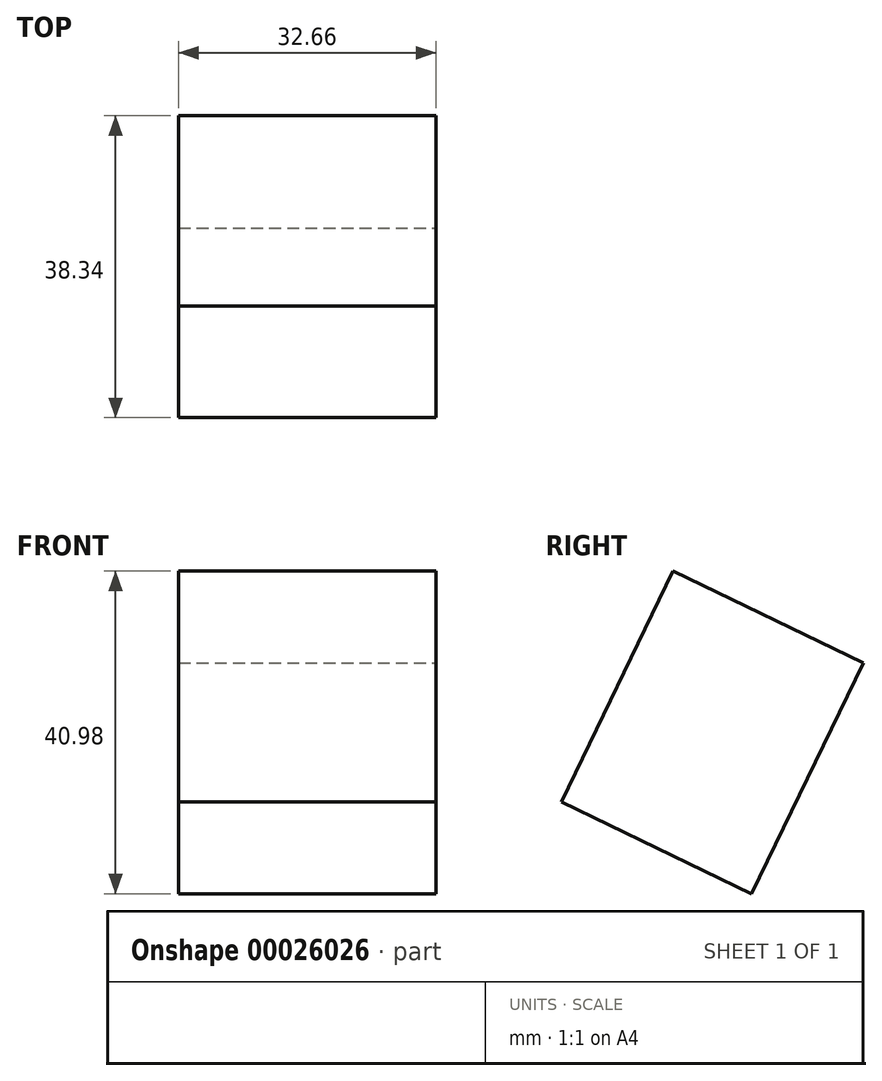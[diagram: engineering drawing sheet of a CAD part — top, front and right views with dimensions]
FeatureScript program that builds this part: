
annotation { "Feature Type Name" : "Feature", "Feature Type Description" : "" }
export const myFeature = defineFeature(function(context is Context, id is Id, definition is map)
    precondition{}
    {
        {
            var Q0;
            Q0=qCreatedBy(makeId("Right.planeOp"),FACE);
            var sketch = newSketch(context, id + "F0", { "sketchPlane" : qUnion([Q0])});
            skLineSegment(sketch, "E0", {"start": v(-66.15, 37.6) * mm, "end": v(-41.97, 25.94) * mm});
            skLineSegment(sketch, "E1", {"start": v(-66.15, 37.6) * mm, "end": v(-80.31, 8.26) * mm});
            skLineSegment(sketch, "E2", {"start": v(-80.31, 8.26) * mm, "end": v(-56.2, -3.37) * mm});
            skLineSegment(sketch, "E3", {"start": v(-41.97, 25.94) * mm, "end": v(-56.2, -3.37) * mm});
            skSolve(sketch);
        }
        {
            var Q0;
            Q0=makeQuery(id+"F0.imprint","IMPRINT",FACE,{"disambiguationData":[TD([[makeQuery(id+"F0.imprint","IMPRINT",EDGE,{"derivedFrom":sQuery(id+"F0.wireOp",EDGE,"E0")}),-1.0]])]});
            extrude(context, id + "F1", {"entities" : qUnion([Q0]), "oppositeDirection" : true, "depth" : 32.66 * mm});
        }
    });
